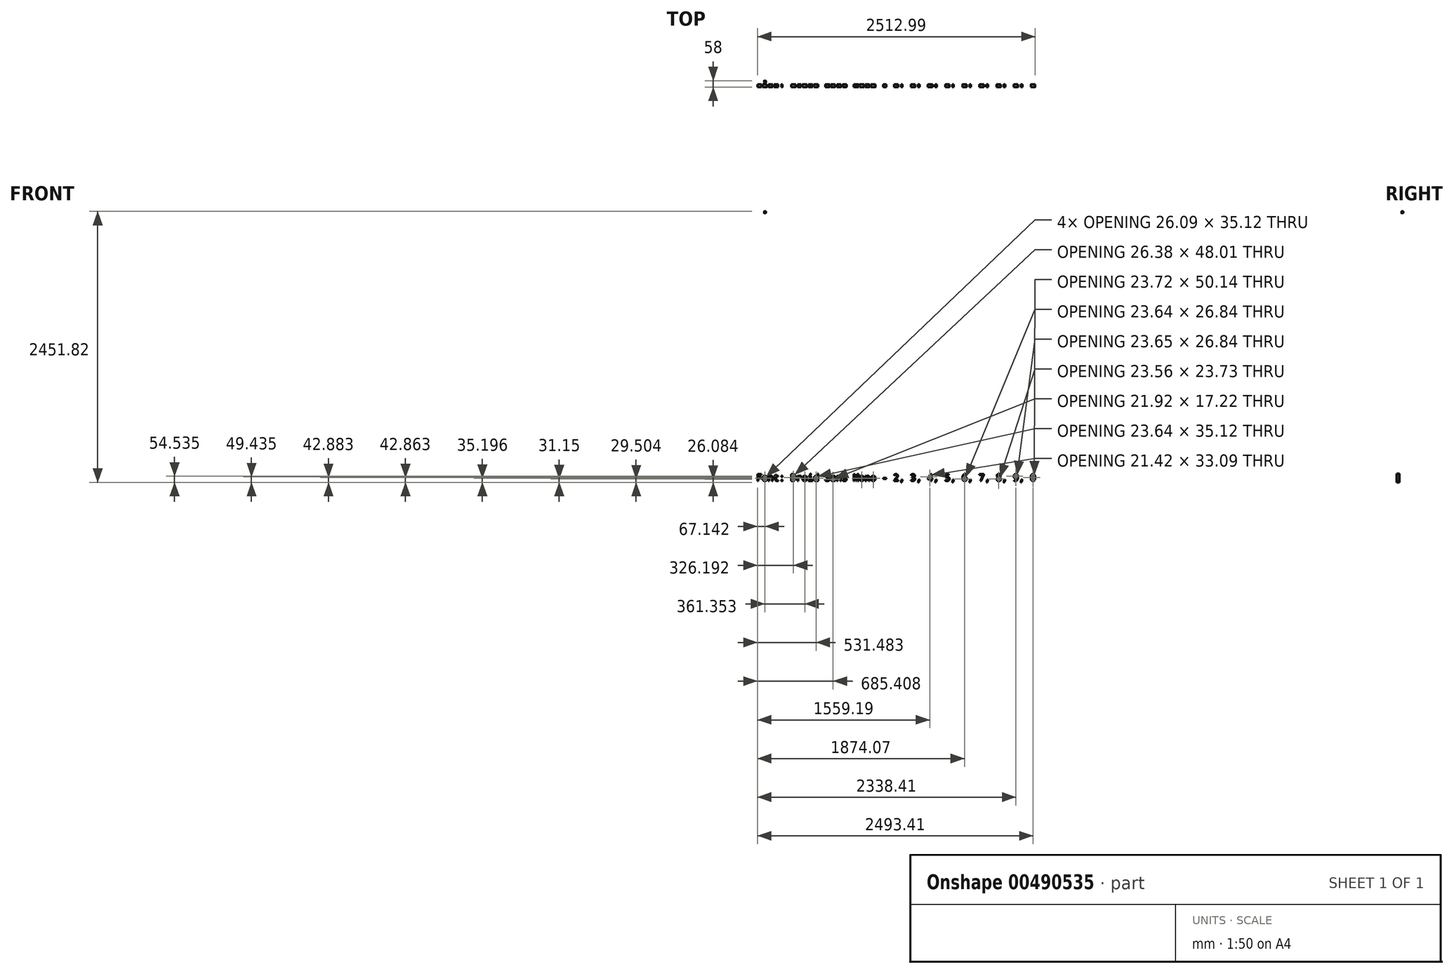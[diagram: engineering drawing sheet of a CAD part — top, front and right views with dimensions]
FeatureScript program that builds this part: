
annotation { "Feature Type Name" : "Feature", "Feature Type Description" : "" }
export const myFeature = defineFeature(function(context is Context, id is Id, definition is map)
    precondition{}
    {
        {
            var Q0;
            Q0=qCreatedBy(makeId("Top.planeOp"),FACE);
            var sketch = newSketch(context, id + "F0", { "sketchPlane" : qUnion([Q0])});
            skLineSegment(sketch, "E0.bottom", {"start": v(8, -8) * mm, "end": v(-8, -8) * mm});
            skLineSegment(sketch, "E0.top", {"start": v(8, 8) * mm, "end": v(-8, 8) * mm});
            skLineSegment(sketch, "E0.left", {"start": v(8, -8) * mm, "end": v(8, 8) * mm});
            skLineSegment(sketch, "E0.right", {"start": v(-8, -8) * mm, "end": v(-8, 8) * mm});
            skPoint(sketch, "E0.middle", {"position": v(0, 0) * mm});
            skSolve(sketch);
        }
        {
            var Q0;
            Q0=qCreatedBy(makeId("Top.planeOp"),FACE);
            var sketch = newSketch(context, id + "F1", { "sketchPlane" : qUnion([Q0])});
            skLineSegment(sketch, "E1.bottom", {"start": v(8, -8) * mm, "end": v(-8, -8) * mm});
            skLineSegment(sketch, "E1.top", {"start": v(8, 8) * mm, "end": v(-8, 8) * mm});
            skLineSegment(sketch, "E1.left", {"start": v(8, -8) * mm, "end": v(8, 8) * mm});
            skLineSegment(sketch, "E1.right", {"start": v(-8, -8) * mm, "end": v(-8, 8) * mm});
            skPoint(sketch, "E1.middle", {"position": v(0, 0) * mm});
            skSolve(sketch);
        }
        {
            var Q0;
            Q0=qSketchRegion(id+"F0",true);
            extrude(context, id + "F2", {"entities" : qUnion([Q0]), "depth" : 8 * mm});
        }
        {
            var Q0;
            Q0=qSketchRegion(id+"F1",true);
            extrude(context, id + "F3", {"entities" : qUnion([Q0]), "operationType" : NewBodyOperationType.ADD, "oppositeDirection" : true, "depth" : 8 * mm});
        }
        {
            var Q0;
            Q0=qCreatedBy(makeId("Front.planeOp"),FACE);
            cPlane(context, id + "F4", {"entities" : qUnion([Q0]), "cplaneType" : CPlaneType.OFFSET, "offset" : 8 * mm, "width" : 150 * mm, "height" : 150 * mm});
        }
        {
            var Q0;
            Q0=qCreatedBy(makeId("Right.planeOp"),FACE);
            cPlane(context, id + "F5", {"entities" : qUnion([Q0]), "cplaneType" : CPlaneType.OFFSET, "offset" : 8 * mm, "width" : 150 * mm, "height" : 150 * mm});
        }
        {
            var Q0;
            Q0=makeQuery(id+"F3.boolean.opBoolean","MERGE",FACE,{"derivedFrom":[makeQuery(id+"F2.opExtrude","SWEPT_FACE",FACE,{"disambiguationData":[OSD([sQuery(id+"F0.wireOp",EDGE,"E0.top")])]}),makeQuery(id+"F3.opExtrude","SWEPT_FACE",FACE,{"disambiguationData":[OSD([sQuery(id+"F1.wireOp",EDGE,"E1.top")])]})]});
            cPlane(context, id + "F6", {"entities" : qUnion([Q0]), "cplaneType" : CPlaneType.OFFSET, "offset" : 0 * mm, "width" : 150 * mm, "height" : 150 * mm});
        }
        {
            var Q0;
            Q0=makeQuery(id+"F3.boolean.opBoolean","MERGE",FACE,{"derivedFrom":[makeQuery(id+"F2.opExtrude","SWEPT_FACE",FACE,{"disambiguationData":[OSD([sQuery(id+"F0.wireOp",EDGE,"E0.right")])]}),makeQuery(id+"F3.opExtrude","SWEPT_FACE",FACE,{"disambiguationData":[OSD([sQuery(id+"F1.wireOp",EDGE,"E1.right")])]})]});
            cPlane(context, id + "F7", {"entities" : qUnion([Q0]), "cplaneType" : CPlaneType.OFFSET, "offset" : 0 * mm, "width" : 150 * mm, "height" : 150 * mm});
        }
        {
            var Q0;
            Q0=makeQuery(id+"F2.opExtrude","CAP_FACE",FACE,{"disambiguationData":[OSD([sQuery(id+"F0.wireOp",EDGE,"E0.bottom"),sQuery(id+"F0.wireOp",EDGE,"E0.top"),sQuery(id+"F0.wireOp",EDGE,"E0.left"),sQuery(id+"F0.wireOp",EDGE,"E0.right")])],"isStart":false});
            cPlane(context, id + "F8", {"entities" : qUnion([Q0]), "cplaneType" : CPlaneType.OFFSET, "offset" : 0 * mm, "width" : 150 * mm, "height" : 150 * mm});
        }
        {
            var Q0;
            Q0=makeQuery(id+"F3.opExtrude","CAP_FACE",FACE,{"disambiguationData":[OSD([sQuery(id+"F1.wireOp",EDGE,"E1.bottom"),sQuery(id+"F1.wireOp",EDGE,"E1.top"),sQuery(id+"F1.wireOp",EDGE,"E1.left"),sQuery(id+"F1.wireOp",EDGE,"E1.right")])],"isStart":false});
            cPlane(context, id + "F9", {"entities" : qUnion([Q0]), "cplaneType" : CPlaneType.OFFSET, "offset" : 0 * mm, "width" : 150 * mm, "height" : 150 * mm});
        }
        {
            var Q0;
            Q0=qCreatedBy(id+"F4.planeOp",FACE);
            var sketch = newSketch(context, id + "F10", { "sketchPlane" : qUnion([Q0])});
            skText(sketch, "E2", { "text": "1/2", "fontName": "OpenSans-Bold.ttf"});
            const initialGuessF10  = {"E2": [-0.007, -0.00317, 1, 0, 0.00635]};
            skSetInitialGuess(sketch, initialGuessF10);
            skSolve(sketch);
        }
        {
            var Q0;
            Q0=qCreatedBy(id+"F5.planeOp",FACE);
            var sketch = newSketch(context, id + "F11", { "sketchPlane" : qUnion([Q0])});
            skText(sketch, "E3", { "text": "2/3", "fontName": "OpenSans-Bold.ttf"});
            const initialGuessF11  = {"E3": [-0.0069, -0.00317, 1, 0, 0.00638]};
            skSetInitialGuess(sketch, initialGuessF11);
            skSolve(sketch);
        }
        {
            var Q0;
            Q0=qCreatedBy(id+"F6.planeOp",FACE);
            var sketch = newSketch(context, id + "F12", { "sketchPlane" : qUnion([Q0])});
            skText(sketch, "E4", { "text": "3/4", "fontName": "OpenSans-Bold.ttf"});
            const initialGuessF12  = {"E4": [-0.007, -0.00317, 1, 0, 0.00628]};
            skSetInitialGuess(sketch, initialGuessF12);
            skSolve(sketch);
        }
        {
            var Q0;
            Q0=qCreatedBy(id+"F7.planeOp",FACE);
            var sketch = newSketch(context, id + "F13", { "sketchPlane" : qUnion([Q0])});
            skText(sketch, "E5", { "text": "4/5", "fontName": "OpenSans-Bold.ttf"});
            const initialGuessF13  = {"E5": [-0.00675, -0.00317, 1, 0, 0.0064]};
            skSetInitialGuess(sketch, initialGuessF13);
            skSolve(sketch);
        }
        {
            var Q0;
            Q0=qCreatedBy(id+"F8.planeOp",FACE);
            var sketch = newSketch(context, id + "F14", { "sketchPlane" : qUnion([Q0])});
            skText(sketch, "E6", { "text": "5/6", "fontName": "OpenSans-Bold.ttf"});
            const initialGuessF14  = {"E6": [-0.00317, 0.007, 0, -1, 0.00635]};
            skSetInitialGuess(sketch, initialGuessF14);
            skSolve(sketch);
        }
        {
            var Q0;
            Q0=qCreatedBy(id+"F9.planeOp",FACE);
            var sketch = newSketch(context, id + "F15", { "sketchPlane" : qUnion([Q0])});
            skText(sketch, "E7", { "text": "6/7", "fontName": "OpenSans-Bold.ttf"});
            const initialGuessF15  = {"E7": [0.00317, -0.0069, 0, 1, 0.00635]};
            skSetInitialGuess(sketch, initialGuessF15);
            skSolve(sketch);
        }
        {
            var Q0;
            Q0=makeQuery(id+"F3.boolean.opBoolean","MERGE",FACE,{"derivedFrom":[makeQuery(id+"F2.opExtrude","SWEPT_FACE",FACE,{"disambiguationData":[OSD([sQuery(id+"F0.wireOp",EDGE,"E0.top")])]}),makeQuery(id+"F3.opExtrude","SWEPT_FACE",FACE,{"disambiguationData":[OSD([sQuery(id+"F1.wireOp",EDGE,"E1.top")])]})]});
            var Q1;
            Q1=makeQuery(id+"F3.boolean.opBoolean","MERGE",FACE,{"derivedFrom":[makeQuery(id+"F2.opExtrude","SWEPT_FACE",FACE,{"disambiguationData":[OSD([sQuery(id+"F0.wireOp",EDGE,"E0.bottom")])]}),makeQuery(id+"F3.opExtrude","SWEPT_FACE",FACE,{"disambiguationData":[OSD([sQuery(id+"F1.wireOp",EDGE,"E1.bottom")])]})]});
            var Q2;
            Q2=makeQuery(id+"F3.boolean.opBoolean","MERGE",FACE,{"derivedFrom":[makeQuery(id+"F2.opExtrude","SWEPT_FACE",FACE,{"disambiguationData":[OSD([sQuery(id+"F0.wireOp",EDGE,"E0.right")])]}),makeQuery(id+"F3.opExtrude","SWEPT_FACE",FACE,{"disambiguationData":[OSD([sQuery(id+"F1.wireOp",EDGE,"E1.right")])]})]});
            var Q3;
            Q3=makeQuery(id+"F3.boolean.opBoolean","MERGE",FACE,{"derivedFrom":[makeQuery(id+"F2.opExtrude","SWEPT_FACE",FACE,{"disambiguationData":[OSD([sQuery(id+"F0.wireOp",EDGE,"E0.left")])]}),makeQuery(id+"F3.opExtrude","SWEPT_FACE",FACE,{"disambiguationData":[OSD([sQuery(id+"F1.wireOp",EDGE,"E1.left")])]})]});
            fillet(context, id + "F16", {"entities" : qUnion([Q0, Q1, Q2, Q3]), "radius" : 1.2 * mm, "tangentPropagation" : true, "allowEdgeOverflow" : false});
        }
        {
            var Q0;
            Q0=qSketchRegion(id+"F10",true);
            extrude(context, id + "F17", {"entities" : qUnion([Q0]), "operationType" : NewBodyOperationType.REMOVE, "oppositeDirection" : true, "depth" : 1.5 * mm});
        }
        {
            var Q0;
            Q0=qSketchRegion(id+"F11",true);
            extrude(context, id + "F18", {"entities" : qUnion([Q0]), "operationType" : NewBodyOperationType.REMOVE, "oppositeDirection" : true, "depth" : 1.5 * mm});
        }
        {
            var Q0;
            Q0=qSketchRegion(id+"F12",true);
            extrude(context, id + "F19", {"entities" : qUnion([Q0]), "operationType" : NewBodyOperationType.REMOVE, "oppositeDirection" : true, "depth" : 1.5 * mm});
        }
        {
            var Q0;
            Q0=qSketchRegion(id+"F13",true);
            extrude(context, id + "F20", {"entities" : qUnion([Q0]), "operationType" : NewBodyOperationType.REMOVE, "oppositeDirection" : true, "depth" : 1.5 * mm});
        }
        {
            var Q0;
            Q0=qSketchRegion(id+"F14",true);
            extrude(context, id + "F21", {"entities" : qUnion([Q0]), "operationType" : NewBodyOperationType.REMOVE, "oppositeDirection" : true, "depth" : 1.5 * mm});
        }
        {
            var Q0;
            Q0=qSketchRegion(id+"F15",true);
            extrude(context, id + "F22", {"entities" : qUnion([Q0]), "operationType" : NewBodyOperationType.REMOVE, "oppositeDirection" : true, "depth" : 1.5 * mm});
        }
        {
            var Q0;
            Q0=qCreatedBy(makeId("Front.planeOp"),FACE);
            cPlane(context, id + "F23", {"entities" : qUnion([Q0]), "cplaneType" : CPlaneType.OFFSET, "offset" : 25 * mm, "width" : 150 * mm, "height" : 150 * mm});
        }
        {
            var Q0;
            Q0=qCreatedBy(id+"F23.planeOp",FACE);
            var sketch = newSketch(context, id + "F24", { "sketchPlane" : qUnion([Q0])});
            skText(sketch, "E8", { "text": "Font: Droid Sans Mono - 2, 3, 4, 5, 6, 7, 8, 9, 0", "fontName": "DroidSansMono.ttf"});
            const initialGuessF24  = {"E8": [-0.07863, -2.43168, 1, 0, 0.06193]};
            skSetInitialGuess(sketch, initialGuessF24);
            skSolve(sketch);
        }
        {
            var Q0;
            Q0 = qSketchRegion(id + "F24", true);
            extrude(context, id + "F25", {"entities" : qUnion([Q0]), "depth" : 25 * mm, "offsetDistance" : 25 * mm});
        }
    });
